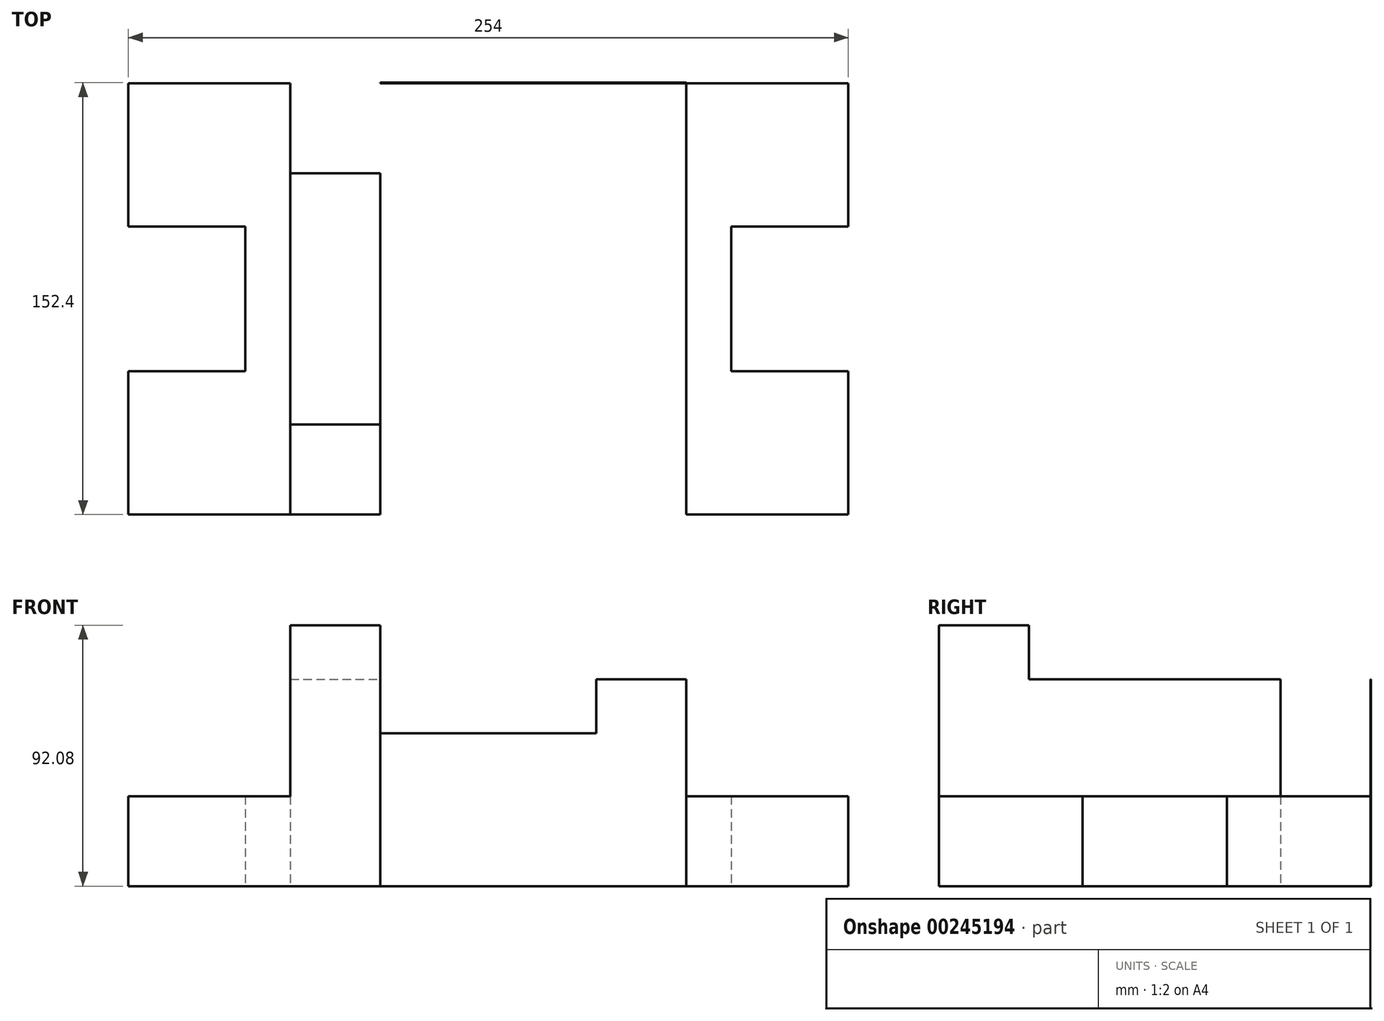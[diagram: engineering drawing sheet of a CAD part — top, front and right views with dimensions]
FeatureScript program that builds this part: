
annotation { "Feature Type Name" : "Feature", "Feature Type Description" : "" }
export const myFeature = defineFeature(function(context is Context, id is Id, definition is map)
    precondition{}
    {
        {
            var Q0;
            Q0=qCreatedBy(makeId("Top.planeOp"),FACE);
            var sketch = newSketch(context, id + "F0", { "sketchPlane" : qUnion([Q0])});
            skLineSegment(sketch, "E0.bottom", {"start": v(-127, 76.12) * mm, "end": v(127, 76.12) * mm});
            skLineSegment(sketch, "E0.top", {"start": v(-127, -76.28) * mm, "end": v(127, -76.28) * mm});
            skLineSegment(sketch, "E0.left", {"start": v(-127, 76.12) * mm, "end": v(-127, 25.32) * mm});
            skLineSegment(sketch, "E0.right", {"start": v(127, 76.12) * mm, "end": v(127, 25.32) * mm});
            skLineSegment(sketch, "E1", {"start": v(127, -25.48) * mm, "end": v(85.72, -25.48) * mm});
            skLineSegment(sketch, "E2", {"start": v(85.72, -25.48) * mm, "end": v(85.72, 25.32) * mm});
            skLineSegment(sketch, "E3", {"start": v(85.73, 25.32) * mm, "end": v(127, 25.32) * mm});
            skLineSegment(sketch, "E4.trimOffspring", {"start": v(127, -25.48) * mm, "end": v(127, -76.28) * mm});
            skLineSegment(sketch, "E5", {"start": v(-127, 25.32) * mm, "end": v(-85.72, 25.32) * mm});
            skLineSegment(sketch, "E6", {"start": v(-85.72, 25.32) * mm, "end": v(-85.72, -25.48) * mm});
            skLineSegment(sketch, "E7", {"start": v(-85.72, -25.48) * mm, "end": v(-127, -25.48) * mm});
            skLineSegment(sketch, "E8.trimOffspring", {"start": v(-127, -25.48) * mm, "end": v(-127, -76.28) * mm});
            skLineSegment(sketch, "E9.bottom", {"start": v(-69.85, 76.12) * mm, "end": v(-38.1, 76.12) * mm});
            skLineSegment(sketch, "E9.top", {"start": v(-69.85, -76.28) * mm, "end": v(-38.1, -76.28) * mm});
            skLineSegment(sketch, "E9.left", {"start": v(-69.85, 76.12) * mm, "end": v(-69.85, -76.28) * mm});
            skLineSegment(sketch, "E9.right", {"start": v(-38.1, 76.12) * mm, "end": v(-38.1, -76.28) * mm});
            skLineSegment(sketch, "E10.bottom", {"start": v(38.1, 76.12) * mm, "end": v(69.85, 76.12) * mm});
            skLineSegment(sketch, "E10.top", {"start": v(38.1, -76.28) * mm, "end": v(69.85, -76.28) * mm});
            skLineSegment(sketch, "E10.left", {"start": v(38.1, 76.12) * mm, "end": v(38.1, -76.28) * mm});
            skLineSegment(sketch, "E10.right", {"start": v(69.85, 76.12) * mm, "end": v(69.85, -76.28) * mm});
            skCircle(sketch, "E11", {"center": v(0, -0.08) * mm, "radius": 15.88 * mm});
            skLineSegment(sketch, "E12.top", {"start": v(-69.85, 44.37) * mm, "end": v(-38.1, 44.37) * mm});
            skLineSegment(sketch, "E12.left", {"start": v(-69.85, 76.12) * mm, "end": v(-69.85, 44.37) * mm});
            skLineSegment(sketch, "E12.right", {"start": v(-38.1, 76.12) * mm, "end": v(-38.1, 44.37) * mm});
            skLineSegment(sketch, "E13.MirrorCS", {"start": v(-69.85, -44.4) * mm, "end": v(-38.1, -44.4) * mm});
            skLineSegment(sketch, "E14.MirrorCS", {"start": v(-69.85, 76.26) * mm, "end": v(-38.1, 76.26) * mm});
            skLineSegment(sketch, "E15.MirrorCS", {"start": v(-69.85, -76.14) * mm, "end": v(-38.1, -76.14) * mm});
            skLineSegment(sketch, "E16.MirrorCS", {"start": v(-38.1, -76.14) * mm, "end": v(-38.1, -44.4) * mm});
            skLineSegment(sketch, "E17.MirrorCS", {"start": v(38.1, 76.26) * mm, "end": v(69.85, 76.26) * mm});
            skLineSegment(sketch, "E18.MirrorCS", {"start": v(38.1, -76.14) * mm, "end": v(69.85, -76.14) * mm});
            skLineSegment(sketch, "E19.MirrorCS", {"start": v(38.1, -76.14) * mm, "end": v(38.1, 76.26) * mm});
            skCircle(sketch, "E20.MirrorC", {"center": v(0, 0.06) * mm, "radius": 15.88 * mm});
            skLineSegment(sketch, "E21.MirrorCS", {"start": v(-85.72, 25.46) * mm, "end": v(-127, 25.46) * mm});
            skLineSegment(sketch, "E22.MirrorCS", {"start": v(-69.85, -76.14) * mm, "end": v(-69.85, -44.4) * mm});
            skLineSegment(sketch, "E23.MirrorCS", {"start": v(-85.72, -25.34) * mm, "end": v(-85.72, 25.46) * mm});
            skLineSegment(sketch, "E24.MirrorCS", {"start": v(-127, -25.34) * mm, "end": v(-85.72, -25.34) * mm});
            skLineSegment(sketch, "E25.MirrorCS", {"start": v(127, 25.46) * mm, "end": v(127, 76.26) * mm});
            skLineSegment(sketch, "E26.MirrorCS", {"start": v(85.73, -25.34) * mm, "end": v(127, -25.34) * mm});
            skLineSegment(sketch, "E27.MirrorCS", {"start": v(-127, 25.46) * mm, "end": v(-127, 76.26) * mm});
            skLineSegment(sketch, "E28.MirrorCS", {"start": v(-38.1, -76.14) * mm, "end": v(-38.1, 76.26) * mm});
            skLineSegment(sketch, "E29.MirrorCS", {"start": v(-127, -76.14) * mm, "end": v(127, -76.14) * mm});
            skLineSegment(sketch, "E30.MirrorCS", {"start": v(69.85, -76.14) * mm, "end": v(69.85, 76.26) * mm});
            skLineSegment(sketch, "E31.MirrorCS", {"start": v(127, 25.46) * mm, "end": v(85.72, 25.46) * mm});
            skLineSegment(sketch, "E32.MirrorCS", {"start": v(127, -76.14) * mm, "end": v(127, -25.34) * mm});
            skLineSegment(sketch, "E33.MirrorCS", {"start": v(85.72, 25.46) * mm, "end": v(85.72, -25.34) * mm});
            skLineSegment(sketch, "E34.MirrorCS", {"start": v(-127, -76.14) * mm, "end": v(-127, -25.34) * mm});
            skLineSegment(sketch, "E35.MirrorCS", {"start": v(-127, 76.26) * mm, "end": v(127, 76.26) * mm});
            skLineSegment(sketch, "E36.MirrorCS", {"start": v(-69.85, -76.14) * mm, "end": v(-69.85, 76.26) * mm});
            skLineSegment(sketch, "E37.top", {"start": v(38.1, 44.5) * mm, "end": v(69.85, 44.5) * mm});
            skLineSegment(sketch, "E37.left", {"start": v(38.1, 76.26) * mm, "end": v(38.1, 44.5) * mm});
            skLineSegment(sketch, "E37.right", {"start": v(69.85, 76.26) * mm, "end": v(69.85, 44.5) * mm});
            skLineSegment(sketch, "E38.bottom", {"start": v(69.85, -76.14) * mm, "end": v(38.1, -76.14) * mm});
            skLineSegment(sketch, "E38.top", {"start": v(69.85, -44.4) * mm, "end": v(38.1, -44.4) * mm});
            skLineSegment(sketch, "E38.left", {"start": v(69.85, -76.14) * mm, "end": v(69.85, -44.4) * mm});
            skLineSegment(sketch, "E38.right", {"start": v(38.1, -76.14) * mm, "end": v(38.1, -44.4) * mm});
            skSolve(sketch);
        }
        {
            var Q0;
            {var subQ7=sQuery(id+"F0.wireOp",EDGE,"E6");Q0=makeQuery(id+"F0.imprint","IMPRINT",FACE,{"disambiguationData":[TD([[makeQuery(id+"F0.imprint","IMPRINT",EDGE,{"derivedFrom":subQ7}),1.0]])]});}
            var Q1;
            {var subQ1=sQuery(id+"F0.wireOp",EDGE,"E1");Q1=makeQuery(id+"F0.imprint","IMPRINT",FACE,{"disambiguationData":[TD([[makeQuery(id+"F0.imprint","IMPRINT",EDGE,{"derivedFrom":subQ1}),1.0]])]});}
            var Q2;
            Q2=sQuery(id+"F0.wireOp",EDGE,"E0.left");
            var Q3;
            Q3=sQuery(id+"F0.wireOp",EDGE,"E1");
            var Q4;
            Q4=sQuery(id+"F0.wireOp",EDGE,"E2");
            var Q5;
            Q5=sQuery(id+"F0.wireOp",EDGE,"E3");
            var Q6;
            Q6=sQuery(id+"F0.wireOp",EDGE,"E4.trimOffspring");
            var Q7;
            Q7=sQuery(id+"F0.wireOp",EDGE,"E5");
            var Q8;
            Q8=sQuery(id+"F0.wireOp",EDGE,"E6");
            var Q9;
            Q9=sQuery(id+"F0.wireOp",EDGE,"E7");
            var Q10;
            Q10=sQuery(id+"F0.wireOp",EDGE,"E8.trimOffspring");
            var Q11;
            Q11=sQuery(id+"F0.wireOp",EDGE,"E9.bottom");
            var Q12;
            Q12=sQuery(id+"F0.wireOp",EDGE,"E9.top");
            var Q13;
            Q13=sQuery(id+"F0.wireOp",EDGE,"E9.left");
            var Q14;
            Q14=sQuery(id+"F0.wireOp",EDGE,"E9.right");
            var Q15;
            Q15=sQuery(id+"F0.wireOp",EDGE,"E10.bottom");
            var Q16;
            Q16=sQuery(id+"F0.wireOp",EDGE,"E10.top");
            var Q17;
            Q17=sQuery(id+"F0.wireOp",EDGE,"E10.left");
            var Q18;
            Q18=sQuery(id+"F0.wireOp",EDGE,"E10.right");
            var Q19;
            Q19=sQuery(id+"F0.wireOp",EDGE,"E11");
            var Q20;
            Q20=sQuery(id+"F0.wireOp",EDGE,"E9.bottom");
            var Q21;
            Q21=sQuery(id+"F0.wireOp",EDGE,"E12.top");
            var Q22;
            Q22=sQuery(id+"F0.wireOp",EDGE,"E12.left");
            var Q23;
            Q23=sQuery(id+"F0.wireOp",EDGE,"E12.right");
            var Q24;
            Q24=sQuery(id+"F0.wireOp",EDGE,"E13.MirrorCS");
            var Q25;
            Q25=sQuery(id+"F0.wireOp",EDGE,"E14.MirrorCS");
            var Q26;
            Q26=sQuery(id+"F0.wireOp",EDGE,"E15.MirrorCS");
            var Q27;
            Q27=sQuery(id+"F0.wireOp",EDGE,"E16.MirrorCS");
            var Q28;
            Q28=sQuery(id+"F0.wireOp",EDGE,"E17.MirrorCS");
            var Q29;
            Q29=sQuery(id+"F0.wireOp",EDGE,"E18.MirrorCS");
            var Q30;
            Q30=sQuery(id+"F0.wireOp",EDGE,"E19.MirrorCS");
            var Q31;
            Q31=sQuery(id+"F0.wireOp",EDGE,"E20.MirrorC");
            var Q32;
            Q32=sQuery(id+"F0.wireOp",EDGE,"E21.MirrorCS");
            var Q33;
            Q33=sQuery(id+"F0.wireOp",EDGE,"E22.MirrorCS");
            var Q34;
            Q34=sQuery(id+"F0.wireOp",EDGE,"E15.MirrorCS");
            var Q35;
            Q35=sQuery(id+"F0.wireOp",EDGE,"E23.MirrorCS");
            var Q36;
            Q36=sQuery(id+"F0.wireOp",EDGE,"E24.MirrorCS");
            var Q37;
            Q37=sQuery(id+"F0.wireOp",EDGE,"E25.MirrorCS");
            var Q38;
            Q38=sQuery(id+"F0.wireOp",EDGE,"E26.MirrorCS");
            var Q39;
            Q39=sQuery(id+"F0.wireOp",EDGE,"E27.MirrorCS");
            var Q40;
            Q40=sQuery(id+"F0.wireOp",EDGE,"E28.MirrorCS");
            var Q41;
            Q41=sQuery(id+"F0.wireOp",EDGE,"E29.MirrorCS");
            var Q42;
            Q42=sQuery(id+"F0.wireOp",EDGE,"E30.MirrorCS");
            var Q43;
            Q43=sQuery(id+"F0.wireOp",EDGE,"E31.MirrorCS");
            var Q44;
            Q44=sQuery(id+"F0.wireOp",EDGE,"E32.MirrorCS");
            var Q45;
            Q45=sQuery(id+"F0.wireOp",EDGE,"E33.MirrorCS");
            var Q46;
            Q46=sQuery(id+"F0.wireOp",EDGE,"E34.MirrorCS");
            var Q47;
            Q47=sQuery(id+"F0.wireOp",EDGE,"E35.MirrorCS");
            var Q48;
            Q48=sQuery(id+"F0.wireOp",EDGE,"E36.MirrorCS");
            var Q49;
            Q49=sQuery(id+"F0.wireOp",EDGE,"E17.MirrorCS");
            var Q50;
            Q50=sQuery(id+"F0.wireOp",EDGE,"E37.top");
            var Q51;
            Q51=sQuery(id+"F0.wireOp",EDGE,"E37.left");
            var Q52;
            Q52=sQuery(id+"F0.wireOp",EDGE,"E37.right");
            var Q53;
            Q53=sQuery(id+"F0.wireOp",EDGE,"E38.bottom");
            var Q54;
            Q54=sQuery(id+"F0.wireOp",EDGE,"E38.top");
            var Q55;
            Q55=sQuery(id+"F0.wireOp",EDGE,"E38.left");
            var Q56;
            Q56=sQuery(id+"F0.wireOp",EDGE,"E38.right");
            extrude(context, id + "F1", {"entities" : qUnion([Q0, Q1]), "surfaceEntities" : qUnion([Q2, Q3, Q4, Q5, Q6, Q7, Q8, Q9, Q10, Q11, Q12, Q13, Q14, Q15, Q16, Q17, Q18, Q19, Q20, Q21, Q22, Q23, Q24, Q25, Q26, Q27, Q28, Q29, Q30, Q31, Q32, Q33, Q34, Q35, Q36, Q37, Q38, Q39, Q40, Q41, Q42, Q43, Q44, Q45, Q46, Q47, Q48, Q49, Q50, Q51, Q52, Q53, Q54, Q55, Q56]), "depth" : 31.75 * mm});
        }
        {
            var Q0;
            {var subQ0=sQuery(id+"F0.wireOp",EDGE,"E13.MirrorCS");Q0=makeQuery(id+"F0.imprint","IMPRINT",FACE,{"disambiguationData":[TD([[makeQuery(id+"F0.imprint","IMPRINT",EDGE,{"derivedFrom":subQ0}),-1.0]])]});}
            var Q1;
            {var subQ0=sQuery(id+"F0.wireOp",EDGE,"E9.bottom");Q1=makeQuery(id+"F0.imprint","IMPRINT",FACE,{"disambiguationData":[TD([[makeQuery(id+"F0.imprint","IMPRINT",EDGE,{"derivedFrom":subQ0}),-1.0]])]});}
            var Q2;
            Q2=makeQuery(id+"F0.imprint","IMPRINT",FACE,{"disambiguationData":[TD([[makeQuery(id+"F0.imprint","IMPRINT",EDGE,{"derivedFrom":sQuery(id+"F0.wireOp",EDGE,"E38.bottom")}),-1.0]])]});
            var Q3;
            {var subQ0=sQuery(id+"F0.wireOp",EDGE,"E10.bottom");Q3=makeQuery(id+"F0.imprint","IMPRINT",FACE,{"disambiguationData":[TD([[makeQuery(id+"F0.imprint","IMPRINT",EDGE,{"derivedFrom":subQ0}),-1.0]])]});}
            extrude(context, id + "F2", {"entities" : qUnion([Q0, Q1, Q2, Q3]), "operationType" : NewBodyOperationType.ADD, "depth" : 92.07 * mm});
        }
        {
            var Q0;
            {var subQ0=sQuery(id+"F0.wireOp",EDGE,"E12.top");Q0=makeQuery(id+"F0.imprint","IMPRINT",FACE,{"disambiguationData":[TD([[makeQuery(id+"F0.imprint","IMPRINT",EDGE,{"derivedFrom":subQ0}),-1.0]])]});}
            var Q1;
            Q1=makeQuery(id+"F0.imprint","IMPRINT",FACE,{"disambiguationData":[TD([[makeQuery(id+"F0.imprint","IMPRINT",EDGE,{"derivedFrom":sQuery(id+"F0.wireOp",EDGE,"E19.MirrorCS")}),-1.0]])]});
            extrude(context, id + "F3", {"entities" : qUnion([Q0, Q1]), "operationType" : NewBodyOperationType.ADD, "depth" : 73.02 * mm});
        }
        {
            var Q0;
            {var subQ7=sQuery(id+"F0.wireOp",EDGE,"E19.MirrorCS");Q0=makeQuery(id+"F0.imprint","IMPRINT",FACE,{"disambiguationData":[TD([[makeQuery(id+"F0.imprint","IMPRINT",EDGE,{"derivedFrom":subQ7}),1.0]])]});}
            extrude(context, id + "F4", {"entities" : qUnion([Q0]), "operationType" : NewBodyOperationType.ADD, "depth" : 53.97 * mm});
        }
    });
